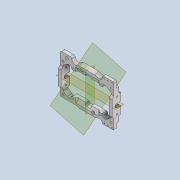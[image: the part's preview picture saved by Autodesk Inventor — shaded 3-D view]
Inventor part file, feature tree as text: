
AUTODESK INVENTOR PART (.ipt)
format: ipt  version: 2020 (Build 240168000, 168)  size: 978,432 bytes
history: native  units: mm
features: sketch x22, extrude x20, projected_geometry x20, reference x17, fillet x14, other x12, mirror x8, thicken_offset x8, plane x3, chamfer x3, hole x2
ambient origin geometry x8: Origin, YZ Plane, XZ Plane, XY Plane, X Axis, Y Axis, Z Axis, Center Point
bodies: Solid1 (feature_tree)
feature tree (129):
  extrude  "Extrusion1"  Depth=30.0mm
  extrude  "Extrusion2"  Depth=56.0mm
  plane  "Work Plane1"
  mirror  "Mirror1"
  extrude  "Extrusion3"  Depth=20.0mm
  extrude  "Extrusion4"  Depth=4.0mm TaperAngle=0.0deg
  plane  "Work Plane2"
  extrude  "Extrusion5"  Depth=10.0mm
  extrude  "Extrusion6"  Depth=1.5mm
  plane  "Work Plane3"
  mirror  "Mirror2"
  extrude  "Extrusion7"  Depth=1.0mm TaperAngle=0.0deg
  mirror  "Mirror3"
  fillet  "Fillet1"  Radius=1.0mm
  thicken_offset  "Thicken1"
  thicken_offset  "Thicken2"
  extrude  "Extrusion8"  Depth=6.0mm TaperAngle=0.0deg
  mirror  "Mirror4"
  extrude  "Extrusion10"  Depth=10.0mm
  thicken_offset  "Thicken3"
  mirror  "Mirror5"
  thicken_offset  "Thicken4"
  extrude  "Extrusion11"  Depth=3.5mm
  extrude  "Extrusion12"  Depth=10.0mm TaperAngle=0.0deg
  fillet  "Fillet4"  Radius=8.0mm
  extrude  "Extrusion13"  Depth=1.0mm
  extrude  "Extrusion14"  Depth=1.0mm
  extrude  "Extrusion15"  Depth=4.0mm
  extrude  "Extrusion16"  Depth=1.0mm
  thicken_offset  "Thicken5"
  fillet  "Fillet7"  Radius=1.5mm
  fillet  "Fillet8"  Radius=4.0mm
  fillet  "Fillet9"  Radius=3.0mm
  fillet  "Fillet10"  Radius=10.0mm
  fillet  "Fillet11"  Radius=4.0mm
  fillet  "Fillet12"  Radius=1.0mm
  extrude  "Extrusion17"  Depth=0.5mm
  mirror  "Mirror6"
  extrude  "Extrusion18"  Depth=10.0mm
  hole  "Hole1"  [1 undecoded]
  extrude  "Extrusion19"  Depth=2.8mm
  thicken_offset  "Thicken6"
  hole  "Hole2"  [1 undecoded]
  extrude  "Extrusion20"  Depth=6.0mm TaperAngle=0.0deg
  extrude  "Extrusion21"  Depth=1.0mm
  mirror  "Mirror7"
  fillet  "Fillet13"  Radius=6.0mm
  mirror  "Mirror8"
  fillet  "Fillet14"  Radius=15.0mm
  fillet  "Fillet15"  Radius=2.8mm
  chamfer  "Chamfer1"  Distance=6.0mm
  fillet  "Fillet16"  Radius=1.5mm
  chamfer  "Chamfer2"  Distance=1.5mm
  chamfer  "Chamfer3"  Distance=4.0mm
  fillet  "Fillet17"  Radius=3.0mm
  fillet  "Fillet18"  Radius=4.0mm
  thicken_offset  "Thicken7"
  thicken_offset  "Thicken8"
  sketch  "Sketch1"  dims[d0=50.0mm d1=30.0mm]
  reference  "Reference1"
  reference  "Reference2"
  sketch  "Sketch2"  dims[d2=36.0mm d3=56.0mm]
  projected_geometry  "Projected Loop1"
  reference  "Reference3"
  sketch  "Sketch3"  dims[d4=4.0mm d5=0.0mm d6=20.0mm]
  reference  "Reference4"
  sketch  "Sketch4"  dims[d7=8.0mm d8=4.0mm d9=0.0mm]
  reference  "Reference5"
  reference  "Reference6"
  sketch  "Sketch5"  dims[d10=10.0mm d11=4.0mm]
  projected_geometry  "Projected Loop2"
  projected_geometry  "Projected Loop3"
  projected_geometry  "Projected Loop4"
  reference  "Reference7"
  sketch  "Sketch6"  dims[d12=80.0mm d13=0.0mm d14=1.5mm]
  projected_geometry  "Projected Loop5"
  projected_geometry  "Projected Loop6"
  sketch  "Sketch7"  dims[d15=1.5mm d16=80.0mm d17=0.0mm d18=1.0mm]
  projected_geometry  "Projected Loop7"
  projected_geometry  "Projected Loop8"
  sketch  "Sketch8"  dims[d19=3.0mm d20=6.0mm d21=0.0mm]
  projected_geometry  "Projected Loop9"
  reference  "Reference8"
  reference  "Reference9"
  sketch  "Sketch10"  dims[d22=10.0mm d23=0.0mm d24=3.5mm]
  projected_geometry  "Projected Loop11"
  sketch  "Sketch11"  dims[d25=5.0mm d26=3.5mm]
  projected_geometry  "Projected Loop13"
  projected_geometry  "Projected Loop14"
  sketch  "Sketch12"  dims[d27=5.0mm d28=10.0mm d29=0.0mm d30=8.0mm]
  reference  "Reference11"
  sketch  "Sketch13"  dims[d32=1.0mm d33=1.0mm]
  projected_geometry  "Projected Loop15"
  sketch  "Sketch14"  dims[d34=1.0mm d35=1.0mm]
  projected_geometry  "Projected Loop16"
  sketch  "Sketch15"  dims[d36=1.5mm d37=4.0mm]
  projected_geometry  "Projected Loop17"
  sketch  "Sketch16"  dims[d38=3.0mm d39=2.0mm d40=1.5mm d41=4.0mm d42=3.0mm d43=10.0mm d44=0.0mm d49=4.0mm d50=0.0mm d51=0.5mm d52=1.0mm]
  reference  "Reference12"
  sketch  "Sketch17"  dims[d53=0.5mm d54=0.5mm]
  projected_geometry  "Projected Loop18"
  sketch  "Sketch18"  dims[d55=10.0mm d56=0.0mm d58=29.0mm]
  reference  "Reference13"
  reference  "Reference14"
  projected_geometry  "Projected Loop19"
  sketch  "Sketch19"  dims[d59=6.0mm d60=0.0mm d61=1.0mm]
  reference  "Reference15"
  sketch  "Sketch20"  dims[d63=2.0mm d64=2.8mm]
  reference  "Reference16"
  projected_geometry  "Projected Loop20"
  sketch  "Sketch21"  dims[d65=6.0mm d66=0.0mm d67=2.0mm]
  reference  "Reference17"
  sketch  "Sketch22"  dims[d68=2.8mm d69=6.0mm d70=0.0mm]
  projected_geometry  "Projected Loop21"
  reference  "Reference18"
  sketch  "Sketch23"  dims[d71=12.0mm d72=5.0mm d73=6.0mm d74=0.0mm d76=15.0mm d78=2.8mm d79=6.0mm d80=0.0mm d81=1.5mm d82=1.5mm d83=4.0mm d84=3.0mm d85=4.0mm d86=1.0mm d87=1.5mm d88=2.0mm d89=1.0mm d90=2.0mm d91=1.1mm d92=2.0mm d93=1.1mm d94=8.0mm d95=0.0mm d96=2.8mm d97=5.0mm d98=2.8mm d99=6.0mm d100=12.0mm d101=0.0mm d102=1.1mm d103=6.0mm d104=4.0mm d105=2.0mm d106=90.0deg d107=100.0mm d108=0.0mm d109=3.0mm d110=4.0mm d111=0.0mm d112=0.005mm d113=0.005mm d114=1.1mm d115=6.0mm d116=4.0mm d117=2.0mm d118=90.0deg d119=100.0mm d120=0.0mm d121=12.0mm d122=4.5mm d123=4.0mm d124=0.0mm d125=3.0mm d126=3.0mm d127=3.0mm d128=2.0mm d129=6.0mm d130=0.0mm d131=3.0mm d132=3.0mm d133=1.0mm d134=2.5mm d135=2.0mm d136=45.0deg d137=2.0mm d138=1.0mm d139=2.0mm d140=45.0deg d141=1.0mm d142=2.0mm d143=45.0deg d144=1.0mm d145=1.0mm d146=1.0mm d147=1.0mm d148=1.0mm d149=1.0mm]
  projected_geometry  "Projected Loop22"
  parser-record x1  (decoder bookkeeping rows leaked as tree rows — omitted from the tree; the rows remain in map.json)
  other  "tip_3_ass.iam"
  other  "bearing_hh_1:1"
  other  "bearing_hh_1:2"
  other  "pin_3_30:2"
  other  "roller_1:2"
  other  "roller_1:1"
  other  "c_roller_1:2"
  other  "c_roller_1:1"
  other  "bw_ass_1:1"
  other  "bw_hl_1:1"
  other  "bw_ass_1:2"
note: 2 required parameter values undecoded (feature->parameter linkage not recoverable at this tier; creation-order binding heuristic only, values carry confidence <= 0.55)
note: 1 file-system path scrubbed to <path> (originals preserved in map.json)
